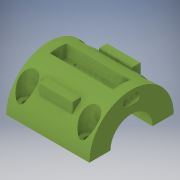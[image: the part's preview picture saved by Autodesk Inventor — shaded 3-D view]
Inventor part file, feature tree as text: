
AUTODESK INVENTOR PART (.ipt)
format: ipt  version: 2018 (Build 220112000, 112)  size: 267,264 bytes
history: native  units: in
note: dims shown in document units (in); Inventor stores cm internally (conversion verified against a paired STEP export)
features: extrude x7, sketch x7, plane x4, fillet x2, mirror x1
ambient origin geometry x8: Origin, YZ Plane, XZ Plane, XY Plane, X Axis, Y Axis, Z Axis, Center Point
bodies: Solid1 (feature_tree)
feature tree (21):
  extrude  "Extrusion1"  Depth=1.9685in TaperAngle=0.0deg
  plane  "Work Plane2"
  plane  "Work Plane6"
  plane  "Work Plane5"
  extrude  "Extrusion17"  Depth=0.7874in TaperAngle=0.0deg
  extrude  "Extrusion18"  Depth=0.2in
  fillet  "Fillet5"  Radius=0.1in
  mirror  "Mirror1"
  fillet  "Fillet6"  Radius=0.3in
  extrude  "Extrusion19"  Depth=0.01in
  extrude  "Extrusion20"  Depth=0.01in
  extrude  "Extrusion21"  Depth=0.2in
  plane  "Work Plane7"
  extrude  "Extrusion22"  Depth=0.992in
  sketch  "Sketch1"  dims[d0=1.0in d9=1.9685in d10=0.0in]
  sketch  "Sketch22"  dims[d176=0.15in d177=0.01in]
  sketch  "Sketch23"  dims[d178=0.5in d179=0.01in]
  sketch  "Sketch24"  dims[d180=0.0in d181=0.2in]
  sketch  "Sketch25"  dims[d182=1.0in d183=0.0in d184=0.992in d185=0.897in d186=0.0475in d187=0.0475in d188=0.33in d189=0.165in d190=0.496in d191=0.075in d192=0.075in d193=0.075in d194=0.075in d195=0.496in d196=0.12in d197=0.0in d198=0.19in d199=0.19in d200=0.19in d201=0.19in d202=0.25in d203=0.25in d204=0.25in d205=0.25in d206=0.25in d207=0.25in d208=0.25in d209=0.25in d210=0.12in d211=0.0in d212=0.5348in d213=0.4in d214=0.4in d215=0.4in d216=0.4in d217=0.5in d218=0.3in d219=0.0in d220=0.0in]
  sketch  "Sketch20"  dims[d153=1.5in d154=0.4in d155=0.3125in d156=0.0in d166=0.7874in d167=0.0in]
  sketch  "Sketch21"  dims[d172=45.0deg d173=0.2in d174=0.1in d175=0.3in]
